# Revit family: 4063812 Feilo Sylvania Lighting Fixtures BRIO IP65VR LED 4K EM SIL  G2
name_source: partatom
category: Lighting Fixtures
revit_build: Autodesk Revit 2017 (Build: 20190507_1515(x64)
units: mm (PartAtom-declared; Revit-internal decimal feet)

## family parameters
Cut with Voids When Loaded = No
Host = Face
Light Source = Yes
OmniClass Number = 23.80.70.00
OmniClass Title = Lighting
Part Type = Normal
Room Calculation Point = No
Round Connector Dimension = Use Diameter
Shared = No

## types (2) — shared parameters
AccessoryMaterial = <By Category>
Assembly Code = D5020200
AssetType = Fixed
BodyMaterial = Body-Sylvania-BrioIP65VR-Silver
ClassificationName = Uniclass2015
ClassificationValue = EF_70_80
Color Filter = 16777215
Default Elevation = 1219 mm
Description = Led exterior bulkhead, Unique feature allowing a choice between High Output or High Efficiency with the flick of a switch, die-cast aluminium body, Vandal resistant, 717/1371LM, 9/17W, 80/81lm/W, 4000K, Driver Current: 350/750mA, CRI80, Non dimmable,Emergency,  IP55,IK10, 50,000hrs (L70), (HxWxD) 358 x 408 x 104mm,  3 step MacAdam ellipse, 3.2kg, RAL 9006, Class 1, 230V,  energy class: A++, A+, A
DiffuserMaterial = Diffuser-Sylvania-BrioIP65VR-Opal
Dimming Lamp Color Temperature Shift = <None>
DocumentationLiterature = http://www.sylvania-lighting.com
DurationUnit = hours
ElectricShockClassification = Class I
Emit Shape Visible in Rendering = No
Emit from Circle Diameter = 300 mm
ExpectedLife = 50000
IfcExportAs = IfcLightFixtureType
IfcExportType = IfcLightFixtureType
ImpactProtectionIndex = IK10
IngressProtection = IP65
InputNominalFrequency = 50/60 Hz
InputVoltage = 230-240V~
Keynote = 16500
Lamp = LED
LampColourRenderingIndex = 80
LampColourTemperature = 4000 K
LampsType = LED
LightOutputRatio = 100
LuminousEfficacy = 72 lm/W
Manufacturer = Feilo Sylvania
ManufacturerName = Feilo Sylvania
Material = aluminium body, polycarbonate diffuser
Model = BRIO IP65VR LED 4K EM SIL  G2
ModelNumber = 4063812
ModelReference = BRIO IP65VR LED 4K EM SIL  G2
Name = BRIO IP65VR LED 4K EM SIL  G2
NominalDepth = 390 mm
NominalHeight = 440 mm
NominalLength = 104 mm
Photometric Web File = 4063812-EM.ies
PowerFactor = 0.98
ReflectorMaterial = <By Category>
Tilt Angle = -90.00°
Type Image = <None>
TypeName = BRIO IP65VR LED 4K EM SIL  G2
URL = http://www.sylvania-lighting.com
Voltage = 230 V
Weight = 3.2 kg
zero-valued in all types: Cost

## per-type parameters (varying)
| type | Apparent Load | LampNominalLuminous | PowerConsumption |
| 4063812 BRIO IP65VR LED 4K EM SIL  G2 High Output High Output | 19 VA | 1371 lm | 19 W |
| 4063812 BRIO IP65VR LED 4K EM SIL  G2 High Efficiency High Efficiency | 11 VA | 717 lm | 11 W |

## geometry (parser evidence)
native form markers: Sweep x2
no freeform markers — native parametric forms only
